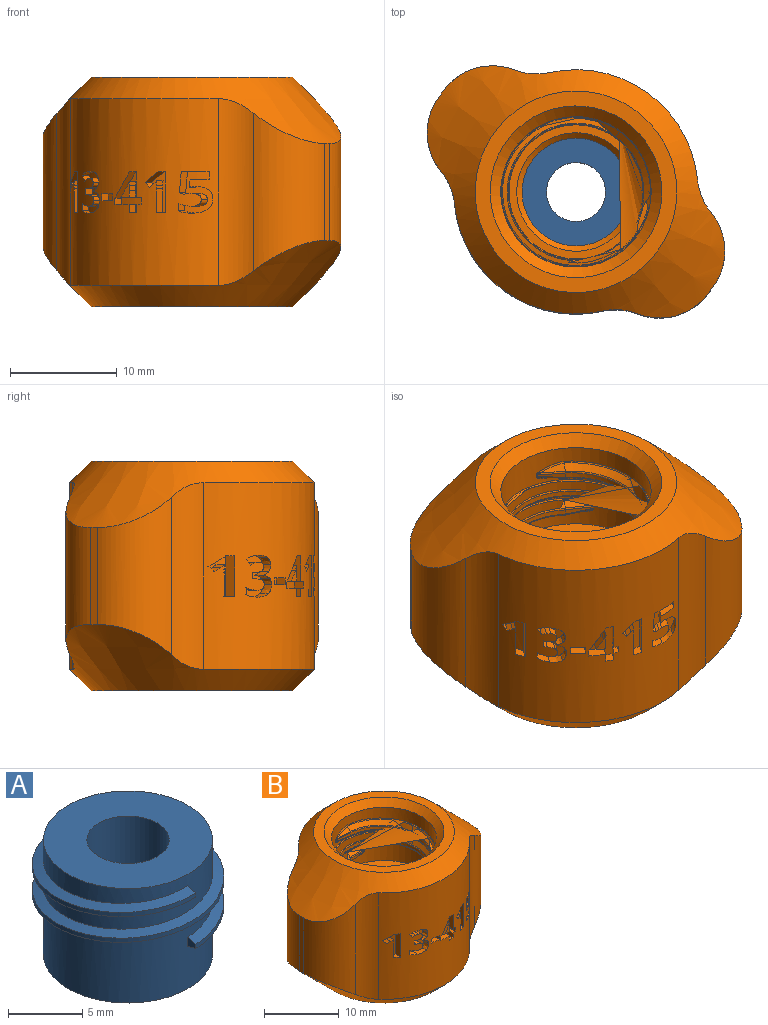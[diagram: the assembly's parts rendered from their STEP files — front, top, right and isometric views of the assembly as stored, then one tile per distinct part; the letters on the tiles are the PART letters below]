
ASSEMBLY  parts=2 mates=1
PART A: 10 faces, bbox 14.9x12.9x9.4 mm
  f0: cylinder r=5.69mm len=11.38mm, axis (0,0,-1), area 174.6mm2, adj f1,f4,f6,f8,f9
  f1: cylinder r=5.69mm len=11.38mm, axis (0,0,-1), area 107.8mm2, adj f0,f3,f5,f8,f9
  f2: cylinder r=2.77mm len=9.42mm, axis (0,0,-1), area 163.9mm2, adj f3,f4
  f3: plane 11.38x11.38mm, normal (0,0,1), area 77.6mm2, adj f1,f2
  f4: plane 11.38x11.38mm, normal (0,0,-1), area 77.6mm2, adj f0,f2
  f5: plane 0.76x0.76mm, normal (1,0,0), area 0.4mm2, adj f1,f7,f8,f9
  f6: plane 0.76x0.76mm, normal (-1,0,0), area 0.4mm2, adj f0,f7,f8,f9
  f7: cylinder r=6.45mm len=12.9mm, axis (0,0,-1), area 28.7mm2, adj f5,f6,f8,f9
  f8: bspline ~14.9x12.9mm, area 60.3mm2, adj f0,f1,f5,f6,f7
  f9: bspline ~14.9x12.9mm, area 60.3mm2, adj f0,f1,f5,f6,f7
PART B: 177 faces, bbox 31.3x31.3x21.5 mm
  f0: cylinder r=11.45mm len=17.49mm, axis (0,0,1), area 309.3mm2, adj f34,f37,f41,f78,f82,f83,f84,f85
  f1: cylinder r=11.45mm len=17.49mm, axis (0,0,1), area 338.4mm2, adj f34,f36,f42,f78
  f2: cylinder r=7.05mm len=14.1mm, axis (0,0,1), area 113mm2, adj f3,f17,f18,f20,f21,f25,f28,f31
  f3: cylinder r=7.05mm len=14.1mm, axis (0,0,1), area 109.3mm2, adj f2,f8,f20,f24,f27,f30,f31,f32
  f4: plane 18.9x18.9mm, normal (0,0,-1), area 77mm2, adj f34,f46
  f5: bspline ~16.29x14.1mm, area 0mm2, adj f12,f13,f17,f19,f20,f24
  f6: bspline ~16.29x14.1mm, area 36.8mm2, adj f10,f15,f26,f28,f31,f33
  f7: cylinder r=6.29mm len=12.58mm, axis (0,0,-1), area 38.5mm2, adj f11,f14,f19,f26
  f8: plane 14.1x14.1mm, normal (0,0,-1), area 59.4mm2, adj f3,f45
  f9: cylinder r=5.05mm len=10.1mm, axis (0,0,-1), area 31.7mm2, adj f45,f79
  f10: plane 1.88x0.43mm, normal (-0.09,0.17,0.98), area 0.5mm2, adj f6,f22,f26,f28
  f11: plane 2.63x0.49mm, normal (-0.09,1,0), area 0.9mm2, adj f7,f16,f19,f21,f22,f26
  f12: plane 2.33x0.62mm, normal (-0.09,0.64,-0.76), area 1.2mm2, adj f5,f16,f17,f19
  f13: plane 2.33x0.62mm, normal (0.09,0.64,-0.76), area 1.2mm2, adj f5,f19,f23,f24
  f14: plane 2.63x0.49mm, normal (0.09,1,0), area 0.9mm2, adj f7,f19,f23,f26,f29,f30
  f15: plane 1.88x0.43mm, normal (0.09,0.17,0.98), area 0.5mm2, adj f6,f26,f29,f33
  f16: cylinder r=0.2mm len=2.63mm, axis (1,0.09,-0.04), area 0.4mm2, adj f11,f12,f18,f19
  f17: bspline ~3.3x1.04mm, area 0.5mm2, adj f2,f5,f12,f18,f20
  f18: bspline ~0.47x0.36mm, area 0.1mm2, adj f2,f16,f17,f21
  f19: bspline ~12.74x12.73mm, area 13.9mm2, adj f5,f7,f11,f12,f13,f14,f16,f23
  f20: bspline ~14.12x14.11mm, area 15.5mm2, adj f2,f3,f5,f17,f24
  f21: cylinder r=0.2mm len=0.19mm, axis (0,0,1), area 0mm2, adj f2,f11,f18,f25
  f22: cylinder r=0.2mm len=2.63mm, axis (0.99,0.09,0.07), area 0.6mm2, adj f10,f11,f25,f26
  f23: cylinder r=0.2mm len=2.63mm, axis (-1,0.09,-0.04), area 0.4mm2, adj f13,f14,f19,f27
  f24: bspline ~2.42x0.77mm, area 0.5mm2, adj f3,f5,f13,f20,f27
  f25: bspline ~1.36x0.5mm, area 0.2mm2, adj f2,f21,f22,f28
  f26: bspline ~12.93x12.92mm, area 22.3mm2, adj f6,f7,f10,f11,f14,f15,f22,f29
  f27: bspline ~0.72x0.44mm, area 0.1mm2, adj f3,f23,f24,f30
  f28: bspline ~1.96x0.43mm, area 0.6mm2, adj f2,f6,f10,f25,f31
  f29: cylinder r=0.2mm len=2.63mm, axis (-0.99,0.09,0.07), area 0.6mm2, adj f14,f15,f26,f32
  f30: cylinder r=0.2mm len=0.19mm, axis (0,0,1), area 0mm2, adj f3,f14,f27,f32
  f31: bspline ~14.13x14.11mm, area 24.6mm2, adj f2,f3,f6,f28,f33
  f32: bspline ~1.12x0.51mm, area 0.2mm2, adj f3,f29,f30,f33
  f33: bspline ~3.34x0.61mm, area 0.6mm2, adj f3,f6,f15,f31,f32
  f34: cone r=9.45mm half-angle=45deg, axis (0,0,1), area 311.7mm2, adj f0,f1,f4,f35,f36,f37,f38,f39
  f35: plane 9.15x0.76mm, normal (-1,0,0), area 6.8mm2, adj f34,f38,f39,f78
  f36: cylinder r=5.69mm len=17.49mm, axis (0,0,1), area 54.1mm2, adj f1,f34,f38,f78
  f37: cylinder r=5.69mm len=17.49mm, axis (0,0,1), area 54.1mm2, adj f0,f34,f39,f78
  f38: cylinder r=5.69mm len=14.78mm, axis (0,0,1), area 89.4mm2, adj f34,f35,f36,f78
  f39: cylinder r=5.69mm len=14.78mm, axis (0,0,1), area 89.4mm2, adj f34,f35,f37,f78
  f40: plane 9.14x0.75mm, normal (1,0,0), area 6.8mm2, adj f34,f43,f44,f78
  f41: cylinder r=5.69mm len=17.49mm, axis (0,0,1), area 54.1mm2, adj f0,f34,f43,f78
  f42: cylinder r=5.69mm len=17.49mm, axis (0,0,1), area 54.1mm2, adj f1,f34,f44,f78
  f43: cylinder r=5.69mm len=14.78mm, axis (0,0,1), area 89.4mm2, adj f34,f40,f41,f78
  f44: cylinder r=5.69mm len=14.78mm, axis (0,0,1), area 89.4mm2, adj f34,f40,f42,f78
  f45: cone r=5.55mm half-angle=45deg, axis (0,0,-1), area 23.6mm2, adj f8,f9
  f46: cone r=7.05mm half-angle=45deg, axis (0,0,-1), area 67.1mm2, adj f2,f4
  f47: cylinder r=7.05mm len=14.1mm, axis (0,0,-1), area 113mm2, adj f48,f61,f62,f64,f65,f69,f72,f75
  f48: cylinder r=7.05mm len=14.1mm, axis (0,0,-1), area 109.3mm2, adj f47,f53,f64,f68,f71,f74,f75,f76
  f49: plane 18.9x18.9mm, normal (0,0,1), area 77mm2, adj f78,f80
  f50: bspline ~16.29x14.1mm, area 0mm2, adj f56,f57,f61,f63,f64,f68
  f51: bspline ~16.29x14.1mm, area 36.8mm2, adj f54,f59,f70,f72,f75,f77
  f52: cylinder r=6.29mm len=12.58mm, axis (0,0,1), area 38.5mm2, adj f55,f58,f63,f70
  f53: plane 14.1x14.1mm, normal (0,0,1), area 59.4mm2, adj f48,f79
  f54: plane 1.88x0.43mm, normal (-0.09,-0.17,-0.98), area 0.5mm2, adj f51,f66,f70,f72
  f55: plane 2.63x0.49mm, normal (-0.09,-1,0), area 0.9mm2, adj f52,f60,f63,f65,f66,f70
  f56: plane 2.33x0.62mm, normal (-0.09,-0.64,0.76), area 1.2mm2, adj f50,f60,f61,f63
  f57: plane 2.33x0.62mm, normal (0.09,-0.64,0.76), area 1.2mm2, adj f50,f63,f67,f68
  f58: plane 2.63x0.49mm, normal (0.09,-1,0), area 0.9mm2, adj f52,f63,f67,f70,f73,f74
  f59: plane 1.88x0.43mm, normal (0.09,-0.17,-0.98), area 0.5mm2, adj f51,f70,f73,f77
  f60: cylinder r=0.2mm len=2.63mm, axis (1,-0.09,0.04), area 0.4mm2, adj f55,f56,f62,f63
  f61: bspline ~3.3x1.04mm, area 0.5mm2, adj f47,f50,f56,f62,f64
  f62: bspline ~0.47x0.36mm, area 0.1mm2, adj f47,f60,f61,f65
  f63: bspline ~12.74x12.73mm, area 13.9mm2, adj f50,f52,f55,f56,f57,f58,f60,f67
  f64: bspline ~14.12x14.11mm, area 15.5mm2, adj f47,f48,f50,f61,f68
  f65: cylinder r=0.2mm len=0.19mm, axis (0,0,-1), area 0mm2, adj f47,f55,f62,f69
  f66: cylinder r=0.2mm len=2.63mm, axis (0.99,-0.09,-0.07), area 0.6mm2, adj f54,f55,f69,f70
  f67: cylinder r=0.2mm len=2.63mm, axis (-1,-0.09,0.04), area 0.4mm2, adj f57,f58,f63,f71
  f68: bspline ~2.42x0.77mm, area 0.5mm2, adj f48,f50,f57,f64,f71
  f69: bspline ~1.36x0.5mm, area 0.2mm2, adj f47,f65,f66,f72
  f70: bspline ~12.93x12.92mm, area 22.3mm2, adj f51,f52,f54,f55,f58,f59,f66,f73
  f71: bspline ~0.72x0.44mm, area 0.1mm2, adj f48,f67,f68,f74
  f72: bspline ~1.96x0.43mm, area 0.6mm2, adj f47,f51,f54,f69,f75
  f73: cylinder r=0.2mm len=2.63mm, axis (-0.99,-0.09,-0.07), area 0.6mm2, adj f58,f59,f70,f76
  f74: cylinder r=0.2mm len=0.19mm, axis (0,0,-1), area 0mm2, adj f48,f58,f71,f76
  f75: bspline ~14.13x14.11mm, area 24.6mm2, adj f47,f48,f51,f72,f77
  f76: bspline ~1.12x0.51mm, area 0.2mm2, adj f48,f73,f74,f77
  f77: bspline ~3.34x0.61mm, area 0.6mm2, adj f48,f51,f59,f75,f76
  f78: cone r=9.45mm half-angle=45deg, axis (0,0,-1), area 311.7mm2, adj f0,f1,f35,f36,f37,f38,f39,f40
  f79: cone r=5.55mm half-angle=45deg, axis (0,0,1), area 23.6mm2, adj f9,f53
  f80: cone r=7.05mm half-angle=45deg, axis (0,0,1), area 67.1mm2, adj f47,f49
  f81: cylinder r=11.45mm len=3.93mm, axis (0,0,1), area 5.9mm2, adj f82,f83,f84,f85,f86,f87,f88,f89
  f82: extruded ~1.09x0.67mm, area 0.8mm2, adj f0,f81,f83,f107
  f83: extruded ~1.31x0.94mm, area 1mm2, adj f0,f81,f82,f84
  f84: extruded ~1.56x1.25mm, area 1.3mm2, adj f0,f81,f83,f85
  f85: plane 1.19x0.56mm, normal (0.83,0,0.56), area 0.7mm2, adj f0,f81,f84,f86
  f86: extruded ~1.2x0.43mm, area 0.5mm2, adj f0,f81,f85,f87
  f87: extruded ~1.16x0.38mm, area 0.4mm2, adj f0,f81,f86,f88
  f88: extruded ~1.19x0.54mm, area 0.8mm2, adj f0,f81,f87,f89
  f89: extruded ~1.07x0.4mm, area 0.5mm2, adj f0,f81,f88,f90
  f90: extruded ~1.25x0.65mm, area 0.7mm2, adj f0,f81,f89,f91
  f91: plane 1.13x0.3mm, normal (0,0,-1), area 0.3mm2, adj f0,f81,f90,f92
  f92: plane 1x0.62mm, normal (1,0,0), area 0.6mm2, adj f0,f81,f91,f93
  f93: plane 1.13x0.29mm, normal (0,0,1), area 0.3mm2, adj f0,f81,f92,f94
  f94: extruded ~1.27x0.7mm, area 0.7mm2, adj f0,f81,f93,f95
  f95: extruded ~1.07x0.38mm, area 0.5mm2, adj f0,f81,f94,f96
  f96: extruded ~1.06x0.44mm, area 0.5mm2, adj f0,f81,f95,f97
  f97: extruded ~1.22x0.59mm, area 0.6mm2, adj f0,f81,f96,f98
  f98: extruded ~1.23x0.53mm, area 0.5mm2, adj f0,f81,f97,f99
  f99: extruded ~1.24x0.49mm, area 0.5mm2, adj f0,f81,f98,f100
  f100: plane 1x0.69mm, normal (1,0,0), area 0.7mm2, adj f0,f81,f99,f101
  f101: extruded ~1.5x1.1mm, area 1.1mm2, adj f0,f81,f100,f102
  f102: extruded ~1.38x1.14mm, area 1.2mm2, adj f0,f81,f101,f103
  f103: extruded ~1.1x0.86mm, area 1mm2, adj f0,f81,f102,f104
  f104: extruded ~1.06x0.6mm, area 0.7mm2, adj f0,f81,f103,f105
  f105: extruded ~1.21x0.7mm, area 0.8mm2, adj f0,f81,f104,f106
  f106: plane 1x0.02mm, normal (-1,0,0), area 0mm2, adj f0,f81,f105,f108
  f107: extruded ~1.06x0.61mm, area 0.7mm2, adj f0,f81,f82,f108
  f108: extruded ~1.18x0.61mm, area 0.7mm2, adj f0,f81,f106,f107
  f109: cylinder r=11.45mm len=1.41mm, axis (0,0,1), area 0.9mm2, adj f110,f111,f112,f113
  f110: plane 1.41x1.2mm, normal (0,0,1), area 1.4mm2, adj f0,f109,f111,f112
  f111: plane 1x0.65mm, normal (-1,0,0), area 0.7mm2, adj f0,f109,f110,f113
  f112: plane 1x0.65mm, normal (1,0,0), area 0.7mm2, adj f0,f109,f110,f113
  f113: plane 1.41x1.2mm, normal (0,0,-1), area 1.4mm2, adj f0,f109,f111,f112
  f114: cylinder r=11.45mm len=3.83mm, axis (0,0,1), area 4mm2, adj f115,f116,f117,f118,f119,f120,f121,f122
  f115: plane 3.83x1mm, normal (-1,0,0), area 3.8mm2, adj f0,f114,f116,f123
  f116: plane 1.26x0.67mm, normal (0,0,-1), area 0.7mm2, adj f0,f114,f115,f117
  f117: plane 1.38x1.24mm, normal (0.62,0,-0.78), area 1.6mm2, adj f0,f114,f116,f118
  f118: plane 1.1x0.49mm, normal (0.78,0,0.63), area 0.6mm2, adj f0,f114,f117,f119
  f119: plane 1.13x0.44mm, normal (-0.63,0,0.78), area 0.6mm2, adj f0,f114,f118,f120
  f120: extruded ~1.09x0.28mm, area 0.4mm2, adj f0,f114,f119,f121
  f121: plane 1x0.4mm, normal (1,0,-0.03), area 0.4mm2, adj f0,f114,f120,f122
  f122: plane 1x0.36mm, normal (1,0,-0.02), area 0.4mm2, adj f0,f114,f121,f124
  f123: plane 1.31x0.81mm, normal (0,0,1), area 0.8mm2, adj f0,f114,f115,f124
  f124: plane 2.21x1mm, normal (1,0,0), area 2.2mm2, adj f0,f114,f122,f123
  f125: cylinder r=11.45mm len=3.88mm, axis (0,0,1), area 7.3mm2, adj f126,f127,f128,f129,f130,f131,f132,f133
  f126: extruded ~1.29x0.4mm, area 0.4mm2, adj f0,f125,f127,f144
  f127: plane 1.06x0.09mm, normal (0.2,0,-0.98), area 0.1mm2, adj f0,f125,f126,f128
  f128: plane 1.05x0.75mm, normal (-1,0,0.09), area 0.8mm2, adj f0,f125,f127,f129
  f129: plane 2.13x1.37mm, normal (0,0,1), area 1.4mm2, adj f0,f125,f128,f130
  f130: plane 1x0.69mm, normal (-1,0,0), area 0.7mm2, adj f0,f125,f129,f131
  f131: plane 2.59x2.08mm, normal (0,0,-1), area 2.1mm2, adj f0,f125,f130,f132
  f132: plane 1.95x1.09mm, normal (1,0,-0.07), area 2mm2, adj f0,f125,f131,f133
  f133: plane 1.19x0.32mm, normal (0.47,0,0.88), area 0.4mm2, adj f0,f125,f132,f134
  f134: extruded ~1.18x0.27mm, area 0.3mm2, adj f0,f125,f133,f135
  f135: extruded ~1.21x0.31mm, area 0.3mm2, adj f0,f125,f134,f136
  f136: extruded ~1.6x0.77mm, area 1.1mm2, adj f0,f125,f135,f137
  f137: extruded ~1.58x0.74mm, area 1.1mm2, adj f0,f125,f136,f138
  f138: extruded ~1.35x0.52mm, area 0.5mm2, adj f0,f125,f137,f139
  f139: extruded ~1.29x0.48mm, area 0.5mm2, adj f0,f125,f138,f140
  f140: plane 1x0.7mm, normal (1,0,0), area 0.7mm2, adj f0,f125,f139,f141
  f141: extruded ~1.66x1.03mm, area 1.1mm2, adj f0,f125,f140,f142
  f142: extruded ~1.93x1.13mm, area 1.2mm2, adj f0,f125,f141,f143
  f143: extruded ~1.39x0.99mm, area 1.1mm2, adj f0,f125,f142,f145
  f144: extruded ~1.76x0.88mm, area 1mm2, adj f0,f125,f126,f145
  f145: extruded ~1.33x0.85mm, area 0.9mm2, adj f0,f125,f143,f144
  f146: cylinder r=11.45mm len=3.83mm, axis (0,0,1), area 5.6mm2, adj f147,f148,f149,f150,f151,f152,f153,f154
  f147: plane 1.04x0.92mm, normal (0,0,-1), area 0.9mm2, adj f146,f148,f160,f165
  f148: plane 1.06x1.03mm, normal (-0.83,0,0.55), area 1.3mm2, adj f146,f147,f149,f165
  f149: extruded ~1.02x0.42mm, area 0.5mm2, adj f146,f148,f150,f165
  f150: plane 1x0.02mm, normal (0,0,1), area 0mm2, adj f146,f149,f159,f165
  f151: plane 1x0.63mm, normal (-1,0,0), area 0.6mm2, adj f0,f146,f152,f163
  f152: plane 1.08x0.46mm, normal (0,0,-1), area 0.5mm2, adj f0,f146,f151,f153
  f153: plane 2.41x1mm, normal (-1,0,0), area 2.4mm2, adj f0,f146,f152,f154
  f154: plane 1.09x0.75mm, normal (0,0,-1), area 0.7mm2, adj f0,f146,f153,f155
  f155: plane 2.47x1.68mm, normal (0.83,0,-0.56), area 3mm2, adj f0,f146,f154,f156
  f156: plane 1x0.56mm, normal (1,0,0), area 0.6mm2, adj f0,f146,f155,f157
  f157: plane 1.63x1.04mm, normal (0,0,1), area 1.6mm2, adj f0,f146,f156,f158
  f158: plane 1x0.79mm, normal (1,0,0), area 0.8mm2, adj f0,f146,f157,f162
  f159: extruded ~1x0.36mm, area 0.4mm2, adj f146,f150,f161,f165
  f160: plane 1x0.65mm, normal (1,0,0), area 0.6mm2, adj f146,f147,f161,f165
  f161: extruded ~1x0.47mm, area 0.5mm2, adj f146,f159,f160,f165
  f162: plane 1.1x0.79mm, normal (0,0,1), area 0.8mm2, adj f0,f146,f158,f164
  f163: plane 1.08x0.46mm, normal (0,0,1), area 0.5mm2, adj f0,f146,f151,f164
  f164: plane 1x0.79mm, normal (-1,0,0), area 0.8mm2, adj f0,f146,f162,f163
  f165: cylinder r=11.45mm len=1.48mm, axis (0,0,1), area 0.7mm2, adj f147,f148,f149,f150,f159,f160,f161
  f166: cylinder r=11.45mm len=3.83mm, axis (0,0,1), area 4.8mm2, adj f167,f168,f169,f170,f171,f172,f173,f174
  f167: plane 3.83x1mm, normal (-1,0,0), area 3.8mm2, adj f0,f166,f168,f175
  f168: plane 1.48x0.67mm, normal (0,0,-1), area 0.7mm2, adj f0,f166,f167,f169
  f169: plane 2.14x1.26mm, normal (0.62,0,-0.78), area 1.6mm2, adj f0,f166,f168,f170
  f170: plane 1.39x0.49mm, normal (0.78,0,0.63), area 0.6mm2, adj f0,f166,f169,f171
  f171: plane 1.4x0.44mm, normal (-0.63,0,0.78), area 0.6mm2, adj f0,f166,f170,f172
  f172: extruded ~1.23x0.28mm, area 0.4mm2, adj f0,f166,f171,f173
  f173: plane 1.01x0.4mm, normal (1,0,-0.03), area 0.4mm2, adj f0,f166,f172,f174
  f174: plane 1.01x0.36mm, normal (1,0,-0.02), area 0.4mm2, adj f0,f166,f173,f176
  f175: plane 1.59x0.81mm, normal (0,0,1), area 0.8mm2, adj f0,f166,f167,f176
  f176: plane 2.21x1mm, normal (1,0,0), area 2.2mm2, adj f0,f166,f174,f175
PLACE A rot(axis=(0,0,-1),36deg) t=(0.91,0.17,0)mm
PLACE B rot(axis=(0,0,-1),36deg) t=(0.91,0.17,0)mm fixed
MATE cylindrical A.f2 <-> B.f9  axis (0,0,-1) through (0.91,0.17,9.42)mm
